# Revit family: BE_77728_de_DE
name_source: partatom
category: Leuchten
revit_build: Autodesk Revit 2015 (Build: 20160512_0715(x64)
units: mm (PartAtom-declared; Revit-internal decimal feet)

## types (4) — shared parameters
AC/DC = AC/DC
Aktualisierung = 2016-06-22T04:10:56
Anschlussleitung = 10.0 m X05BQ-F 4 × 1²
BEGA_Dummy = Nein
BEGA_IES = Ja
BEGA_Intern = Ja
BEGA_Intern_Konstruktion = Ja
BEGA_Intern_an = Ja
BEGA_Intern_aus = Ja
Beschreibung = Aufsatzleuchte
Beschreibung_Sonderanfertigung = Hier können Sie Informationen zur Sonderanfertigung eintragen.
CE_Konformität = ja
ENEC = ja
Einstecktiefe = 90 mm
Energieeffizienzklasse = LED A++ - A
Farbfilter = 16777215
Farbtemperaturverschiebung bei Dämpfen der Lampe = <Keine Auswahl>
Farbwiedergabeindex = Ra > 80
Frequenz = 0/50-60 Hz
Gewicht = 14.0 kg
Hersteller = BEGA
Lampe = LED 76 W
Lastklassifizierung = Beleuchtung
Lebensdauerkriterien = L70 = 50.000 h
Logo = BEGA_Logo.png
Material_02 = BEGA_Oberfläche_Silber_matt
Material_06 = BEGA_Oberfläche_Edelstahl_gebürstet
Material_09 = BEGA_Glas_klar
Material_11 = BEGA_Glas_opal
Material_15 = BEGA_Leuchtmedium_matt
Material_17 = BEGA_Reflektor
Neigungswinkel = 0.00°
Produktdatenblatt = http://www.bega.de
Scheinlast = 0 VA
Schutzart = IP 66
Schutzklasse = II
Sonderanfertigung = Nein
Spannung = 240 V
Typenbild = 77728.png
URL = http://www.bega.de
Umgebungstemperatur = 25 °C
Windangriffsfläche = 0.13 m²
zero-valued in all types: Vorgabe-Ansicht

## per-type parameters (varying)
| type | Bestellnummer | Datei für fotometrisches Netz | Farbtemperatur | LED_Modulbezeichnung | Lampenlichtstrom | Leuchtenlichtstrom | M_A | M_G | Modell |
| BEGA_77728_Silber_K3 | 77728AK3 | BE_77728K3.IES | 3000 K | 4x LED-0283/830 | 8840 lm | 6890 lm | Ja | Nein | 77728AK3 |
| BEGA_77728_Silber_K4 | 77728A | BE_77728.IES | 4000 K | 4x LED-0283/840 | 9500 lm | 7405 lm | Ja | Nein | 77728A |
| BEGA_77728_Grafit_K3 | 77728K3 | BE_77728K3.IES | 3000 K | 4x LED-0283/830 | 8840 lm | 6890 lm | Nein | Ja | 77728K3 |
| BEGA_77728_Grafit_K4 | 77728 | BE_77728.IES | 4000 K | 4x LED-0283/840 | 9500 lm | 7405 lm | Nein | Ja | 77728 |
